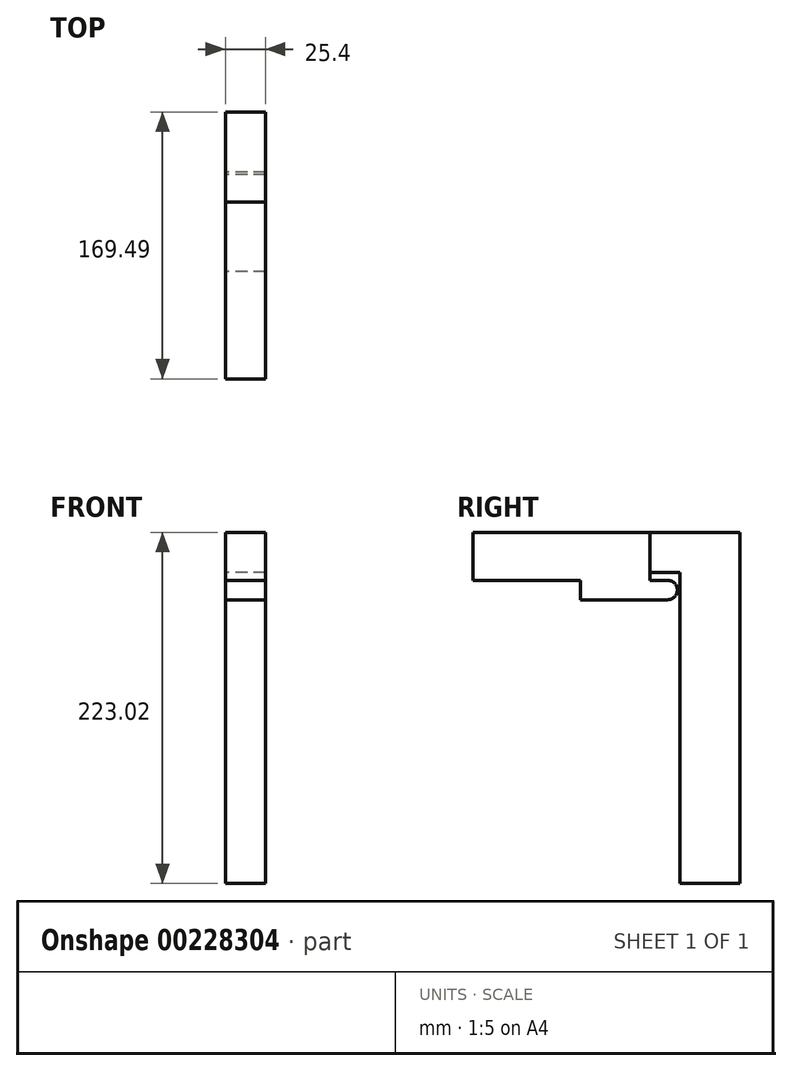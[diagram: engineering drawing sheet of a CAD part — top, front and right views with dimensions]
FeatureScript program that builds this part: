
annotation { "Feature Type Name" : "Feature", "Feature Type Description" : "" }
export const myFeature = defineFeature(function(context is Context, id is Id, definition is map)
    precondition{}
    {
        {
            var Q0;
            Q0=qCreatedBy(makeId("Right.planeOp"),FACE);
            var sketch = newSketch(context, id + "F0", { "sketchPlane" : qUnion([Q0])});
            skLineSegment(sketch, "E0", {"start": v(0, 0) * mm, "end": v(0, 197.62) * mm});
            skLineSegment(sketch, "E1", {"start": v(0, 197.62) * mm, "end": v(-19.05, 197.62) * mm});
            skLineSegment(sketch, "E2", {"start": v(-19.05, 197.62) * mm, "end": v(-19.05, 223.02) * mm});
            skLineSegment(sketch, "E3", {"start": v(-19.05, 223.02) * mm, "end": v(38.2, 223.02) * mm});
            skLineSegment(sketch, "E4", {"start": v(38.2, 223.02) * mm, "end": v(38.2, 0) * mm});
            skLineSegment(sketch, "E5", {"start": v(38.2, 0) * mm, "end": v(0, 0) * mm});
            skLineSegment(sketch, "E6", {"start": v(-19.05, 223.02) * mm, "end": v(-131.3, 223.02) * mm});
            skLineSegment(sketch, "E7", {"start": v(-131.3, 223.02) * mm, "end": v(-131.3, 192.54) * mm});
            skLineSegment(sketch, "E8", {"start": v(-131.3, 192.54) * mm, "end": v(-19.05, 192.54) * mm});
            skLineSegment(sketch, "E9", {"start": v(-19.05, 192.54) * mm, "end": v(-19.05, 197.62) * mm});
            skCircle(sketch, "E10", {"center": v(-7.7, 186.4) * mm, "radius": 6.14 * mm});
            skLineSegment(sketch, "E11", {"start": v(-19.05, 192.54) * mm, "end": v(-7.7, 192.54) * mm});
            skLineSegment(sketch, "E12", {"start": v(-62.98, 192.54) * mm, "end": v(-62.98, 180.26) * mm});
            skLineSegment(sketch, "E13", {"start": v(-62.98, 180.26) * mm, "end": v(-7.7, 180.26) * mm});
            skLineSegment(sketch, "E14.bottom", {"start": v(0, 197.62) * mm, "end": v(-7.7, 197.62) * mm});
            skLineSegment(sketch, "E14.top", {"start": v(0, 180.26) * mm, "end": v(-7.7, 180.26) * mm});
            skLineSegment(sketch, "E14.left", {"start": v(0, 197.62) * mm, "end": v(0, 180.26) * mm});
            skLineSegment(sketch, "E14.right", {"start": v(-7.7, 197.62) * mm, "end": v(-7.7, 180.26) * mm});
            skSolve(sketch);
        }
        {
            var Q0;
            Q0=makeQuery(id+"F0.imprint","IMPRINT",FACE,{"disambiguationData":[TD([[makeQuery(id+"F0.imprint","IMPRINT",EDGE,{"derivedFrom":sQuery(id+"F0.wireOp",EDGE,"E0")}),-1.0]])]});
            var Q1;
            {var subQ1=sQuery(id+"F0.wireOp",EDGE,"E14.bottom");Q1=makeQuery(id+"F0.imprint","IMPRINT",FACE,{"disambiguationData":[TD([[makeQuery(id+"F0.imprint","IMPRINT",EDGE,{"derivedFrom":subQ1}),1.0]])]});}
            extrude(context, id + "F1", {"entities" : qUnion([Q0, Q1]), "depth" : 25.4 * mm});
        }
        {
            var Q0;
            Q0=makeQuery(id+"F0.imprint","IMPRINT",FACE,{"disambiguationData":[TD([[makeQuery(id+"F0.imprint","IMPRINT",EDGE,{"derivedFrom":sQuery(id+"F0.wireOp",EDGE,"E2")}),1.0]])]});
            var Q1;
            {var subQ1=sQuery(id+"F0.wireOp",EDGE,"E11");Q1=makeQuery(id+"F0.imprint","IMPRINT",FACE,{"disambiguationData":[TD([[makeQuery(id+"F0.imprint","IMPRINT",EDGE,{"derivedFrom":subQ1}),-1.0]])]});}
            var Q2;
            {var subQ0=sQuery(id+"F0.wireOp",EDGE,"E14.right");var subQ1=sQuery(id+"F0.wireOp",EDGE,"E10");var subQ2=makeQuery(id+"F0.imprint","INTERSECT",VERTEX,{"derivedFrom":[subQ1,sQuery(id+"F0.wireOp",EDGE,"E11"),subQ0]});Q2=makeQuery(id+"F0.imprint","IMPRINT",FACE,{"disambiguationData":[TD([[makeQuery(id+"F0.imprint","IMPRINT",EDGE,{"disambiguationData":[TD([[subQ2,-1.0]])],"derivedFrom":subQ1}),1.0]])]});}
            var Q3;
            {var subQ0=sQuery(id+"F0.wireOp",EDGE,"E14.right");var subQ1=sQuery(id+"F0.wireOp",EDGE,"E10");var subQ2=makeQuery(id+"F0.imprint","INTERSECT",VERTEX,{"derivedFrom":[subQ1,sQuery(id+"F0.wireOp",EDGE,"E11"),subQ0]});Q3=makeQuery(id+"F0.imprint","IMPRINT",FACE,{"disambiguationData":[TD([[makeQuery(id+"F0.imprint","IMPRINT",EDGE,{"disambiguationData":[TD([[subQ2,1.0]])],"derivedFrom":subQ1}),1.0]])]});}
            extrude(context, id + "F2", {"entities" : qUnion([Q0, Q1, Q2, Q3]), "depth" : 25.4 * mm});
        }
    });
